# Revit family: Wall_Mount_ADA_Cooler-Elkay-LZS8L
name_source: partatom
category: Plumbing Fixtures
units: mm (PartAtom-declared; Revit-internal decimal feet)

## family parameters
Always vertical = Yes
Cut with Voids When Loaded = No
Maintain Annotation Orientation = No
OmniClass Number = 23.65.70.14.11
OmniClass Title = Drinking Fountains/Coolers
Part Type = Normal
Room Calculation Point = No
Round Connector Dimension = Use Diameter
Shared = No
Work Plane-Based = No

## types (1)
- LZS8L(Wall Mount ADA Cooler filtered Refrigerated)
    Activation Method = Electronic Front Bubbler Pushbar
    Approx. Shipping Weight (lbs) = 54
    Assembly Code = D2010.60
    Chilling Capacity(GPH) = 8
    Connector Outlet B = 1.25 "
    Connector Supply A = 0.375 "
    Current = 0 A
    Default Elevation = 0 "
    Description = Wall Mount ADA Cooler Filtered Refrigerated Light Gray Granite
    Inlet Connection Size (inch) = 0.375 "
    Main Material = Finish-Elkay-Steel
    Manufacturer = Elkay Manufacturer Company
    Manufacturer Brand = Elkay (by Zurn Elkay Water Solutions)
    Masking A1 = 21.444 "
    Masking A2 = 21.01 "
    Masking Arc Radius = 21 "
    Material_Shroud = Finish-Elkay-Light Gray
    Material_Wrapper = Finish-Elkay-Light Gray(1)
    Model = LZS8L
    Number of Poles = 1
    Outlet Connection Size (inch) = 1.25
    Power Factor = 1
    Product Documentation Link = https://www.elkayfiles.com
    Product Installation Sheet URL = https://www.elkayfiles.com
    Product Page URL = https://www.elkay.com
    Product Weight (lbs) = 45
    Product data URL = https://bimobject.com
    Repair Parts URL = https://www.elkayfiles.com
    URL = https://www.elkay.com
    Voltage = 115 V

## geometry (parser evidence)
native form markers: Sweep x9
no freeform markers — native parametric forms only
